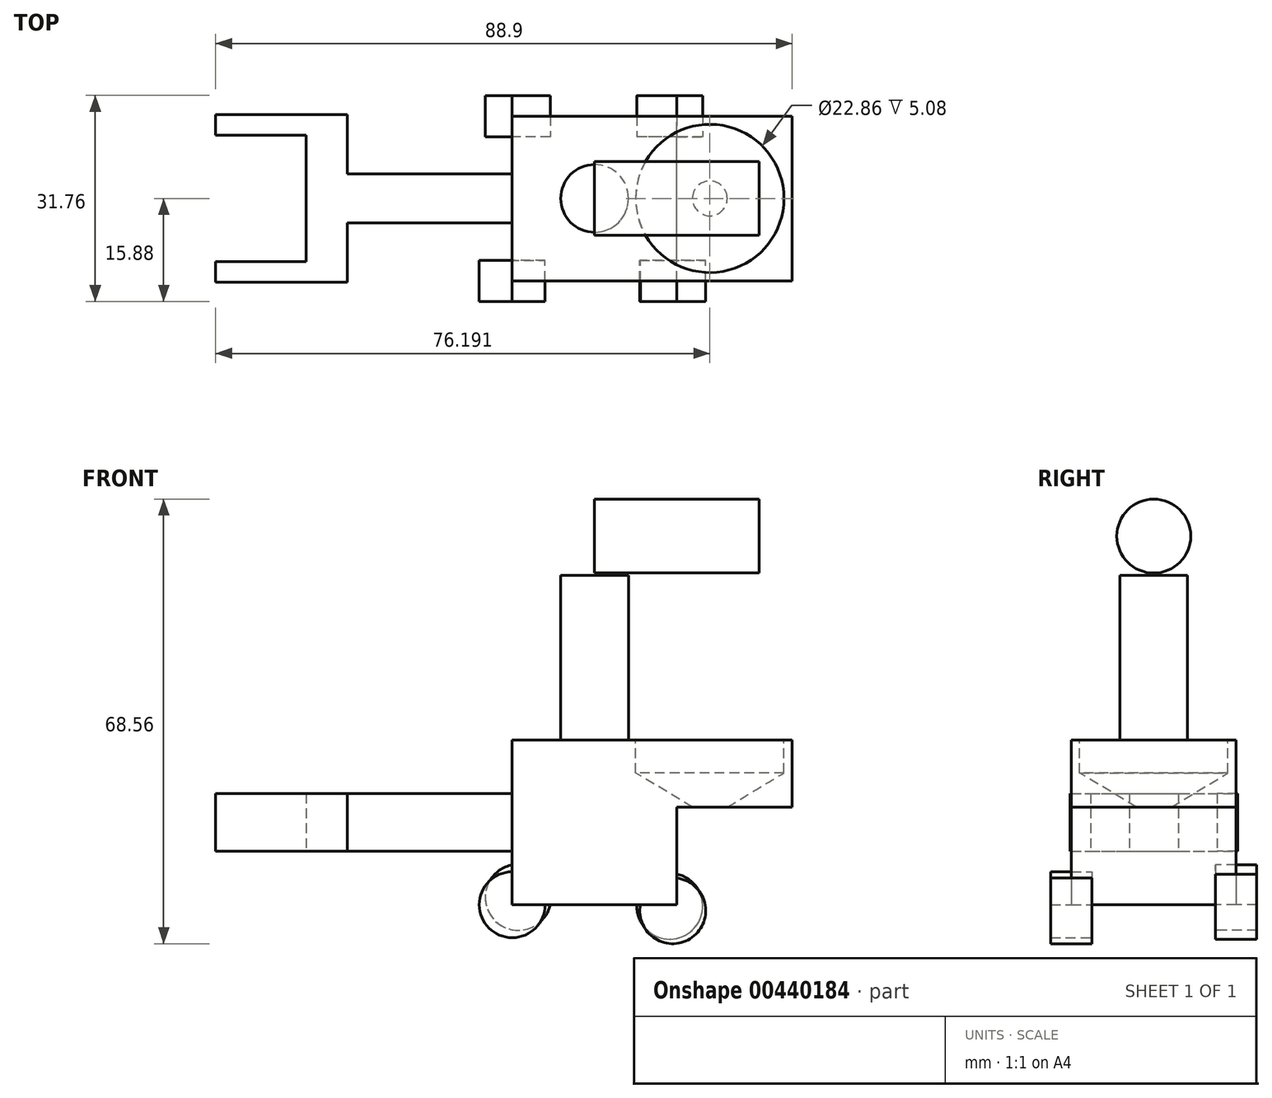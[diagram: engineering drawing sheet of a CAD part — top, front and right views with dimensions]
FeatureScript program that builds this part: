
annotation { "Feature Type Name" : "Feature", "Feature Type Description" : "" }
export const myFeature = defineFeature(function(context is Context, id is Id, definition is map)
    precondition{}
    {
        {
            var Q0;
            Q0=qCreatedBy(makeId("Front.planeOp"),FACE);
            var sketch = newSketch(context, id + "F0", { "sketchPlane" : qUnion([Q0])});
            skLineSegment(sketch, "E0.bottom", {"start": v(12.7, 12.7) * mm, "end": v(-12.7, 12.7) * mm});
            skLineSegment(sketch, "E0.top", {"start": v(12.7, -12.7) * mm, "end": v(-12.7, -12.7) * mm});
            skLineSegment(sketch, "E0.left", {"start": v(12.7, 12.7) * mm, "end": v(12.7, -12.7) * mm});
            skLineSegment(sketch, "E0.right", {"start": v(-12.7, 12.7) * mm, "end": v(-12.7, -12.7) * mm});
            skPoint(sketch, "E0.middle", {"position": v(0, 0) * mm});
            skSolve(sketch);
        }
        {
            var Q0;
            Q0=qSketchRegion(id+"F0",true);
            extrude(context, id + "F1", {"entities" : qUnion([Q0]), "endBound" : BoundingType.SYMMETRIC, "depth" : 25.4 * mm});
        }
        {
            var Q0;
            Q0=makeQuery(id+"F1.opExtrude","CAP_FACE",FACE,{"disambiguationData":[OSD([sQuery(id+"F0.wireOp",EDGE,"E0.bottom"),sQuery(id+"F0.wireOp",EDGE,"E0.top"),sQuery(id+"F0.wireOp",EDGE,"E0.left"),sQuery(id+"F0.wireOp",EDGE,"E0.right")])],"isStart":false});
            var sketch = newSketch(context, id + "F2", { "sketchPlane" : qUnion([Q0])});
            skCircle(sketch, "E1", {"center": v(-12.7, -12.7) * mm, "radius": 5.08 * mm});
            skCircle(sketch, "E2", {"center": v(12.06, -13.63) * mm, "radius": 5.08 * mm});
            skSolve(sketch);
        }
        {
            var Q0;
            {var subQ0=sQuery(id+"F2.wireOp",EDGE,"E1");var subQ1=makeQuery(id+"F1.opExtrude","CAP_EDGE",EDGE,{"disambiguationData":[OSD([sQuery(id+"F0.wireOp",EDGE,"E0.top")])],"isStart":false});var subQ2=makeQuery(id+"F2.imprint","INTERSECT",VERTEX,{"derivedFrom":[subQ1,subQ0]});Q0=makeQuery(id+"F2.imprint","IMPRINT",FACE,{"disambiguationData":[TD([[makeQuery(id+"F2.imprint","IMPRINT",EDGE,{"disambiguationData":[TD([[subQ2,1.0]])],"derivedFrom":subQ0}),1.0]])]});}
            var Q1;
            {var subQ0=sQuery(id+"F2.wireOp",EDGE,"E2");var subQ1=makeQuery(id+"F1.opExtrude","CAP_EDGE",EDGE,{"disambiguationData":[OSD([sQuery(id+"F0.wireOp",EDGE,"E0.top")])],"isStart":false});var subQ2=makeQuery(id+"F2.imprint","INTERSECT",VERTEX,{"derivedFrom":[subQ1,subQ0]});Q1=makeQuery(id+"F2.imprint","IMPRINT",FACE,{"disambiguationData":[TD([[makeQuery(id+"F2.imprint","IMPRINT",EDGE,{"disambiguationData":[TD([[subQ2,-1.0]])],"derivedFrom":subQ0}),1.0]])]});}
            extrude(context, id + "F3", {"entities" : qUnion([Q0, Q1]), "operationType" : NewBodyOperationType.ADD, "endBound" : BoundingType.SYMMETRIC, "depth" : 6.35 * mm});
        }
        {
            var Q0;
            Q0=makeQuery(id+"F1.opExtrude","CAP_FACE",FACE,{"disambiguationData":[OSD([sQuery(id+"F0.wireOp",EDGE,"E0.bottom"),sQuery(id+"F0.wireOp",EDGE,"E0.top"),sQuery(id+"F0.wireOp",EDGE,"E0.left"),sQuery(id+"F0.wireOp",EDGE,"E0.right")])],"isStart":true});
            var sketch = newSketch(context, id + "F4", { "sketchPlane" : qUnion([Q0])});
            skCircle(sketch, "E3", {"center": v(-11.6, -12.93) * mm, "radius": 5.08 * mm});
            skCircle(sketch, "E4", {"center": v(11.78, -11.56) * mm, "radius": 5.08 * mm});
            skSolve(sketch);
        }
        {
            var Q0;
            {var subQ0=sQuery(id+"F4.wireOp",EDGE,"E3");var subQ1=makeQuery(id+"F1.opExtrude","CAP_EDGE",EDGE,{"disambiguationData":[OSD([sQuery(id+"F0.wireOp",EDGE,"E0.top")])],"isStart":true});var subQ2=makeQuery(id+"F4.imprint","INTERSECT",VERTEX,{"derivedFrom":[subQ1,subQ0]});Q0=makeQuery(id+"F4.imprint","IMPRINT",FACE,{"disambiguationData":[TD([[makeQuery(id+"F4.imprint","IMPRINT",EDGE,{"disambiguationData":[TD([[subQ2,1.0]])],"derivedFrom":subQ0}),1.0]])]});}
            var Q1;
            {var subQ0=sQuery(id+"F4.wireOp",EDGE,"E4");var subQ1=makeQuery(id+"F1.opExtrude","CAP_EDGE",EDGE,{"disambiguationData":[OSD([sQuery(id+"F0.wireOp",EDGE,"E0.top")])],"isStart":true});var subQ2=makeQuery(id+"F4.imprint","INTERSECT",VERTEX,{"derivedFrom":[subQ1,subQ0]});Q1=makeQuery(id+"F4.imprint","IMPRINT",FACE,{"disambiguationData":[TD([[makeQuery(id+"F4.imprint","IMPRINT",EDGE,{"disambiguationData":[TD([[subQ2,-1.0]])],"derivedFrom":subQ0}),1.0]])]});}
            extrude(context, id + "F5", {"entities" : qUnion([Q0, Q1]), "operationType" : NewBodyOperationType.ADD, "endBound" : BoundingType.SYMMETRIC, "depth" : 6.35 * mm});
        }
        {
            var Q0;
            Q0=makeQuery(id+"F1.opExtrude","SWEPT_FACE",FACE,{"disambiguationData":[OSD([sQuery(id+"F0.wireOp",EDGE,"E0.bottom")])]});
            var sketch = newSketch(context, id + "F6", { "sketchPlane" : qUnion([Q0])});
            skCircle(sketch, "E5", {"center": v(0, 0) * mm, "radius": 5.22 * mm});
            skSolve(sketch);
        }
        {
            var Q0;
            Q0=makeQuery(id+"F6.imprint","IMPRINT",FACE,{"disambiguationData":[TD([[makeQuery(id+"F6.imprint","IMPRINT",EDGE,{"derivedFrom":sQuery(id+"F6.wireOp",EDGE,"E5")}),1.0]])]});
            extrude(context, id + "F7", {"entities" : qUnion([Q0]), "operationType" : NewBodyOperationType.ADD, "depth" : 25.4 * mm});
        }
        {
            var Q0;
            Q0=qCreatedBy(makeId("Right.planeOp"),FACE);
            var sketch = newSketch(context, id + "F8", { "sketchPlane" : qUnion([Q0])});
            skCircle(sketch, "E6", {"center": v(0, 44.15) * mm, "radius": 5.7 * mm});
            skSolve(sketch);
        }
        {
            var Q0;
            Q0=makeQuery(id+"F8.imprint","IMPRINT",FACE,{"disambiguationData":[TD([[makeQuery(id+"F8.imprint","IMPRINT",EDGE,{"derivedFrom":sQuery(id+"F8.wireOp",EDGE,"E6")}),1.0]])]});
            extrude(context, id + "F9", {"entities" : qUnion([Q0]), "depth" : 25.4 * mm});
        }
        {
            var Q0;
            Q0=makeQuery(id+"F1.opExtrude","SWEPT_FACE",FACE,{"disambiguationData":[OSD([sQuery(id+"F0.wireOp",EDGE,"E0.left")])]});
            var sketch = newSketch(context, id + "F10", { "sketchPlane" : qUnion([Q0])});
            skCircle(sketch, "E7", {"center": v(0, 0) * mm, "radius": 0.9 * mm});
            skSolve(sketch);
        }
        {
            var Q0;
            Q0=sQuery(id+"F10.wireOp",EDGE,"E7");
            extrude(context, id + "F11", {"bodyType" : ToolBodyType.SURFACE, "surfaceEntities" : qUnion([Q0]), "depth" : 25.4 * mm});
        }
        {
            var Q0;
            Q0=makeQuery(id+"F1.opExtrude","SWEPT_FACE",FACE,{"disambiguationData":[OSD([sQuery(id+"F0.wireOp",EDGE,"E0.right")])]});
            var sketch = newSketch(context, id + "F12", { "sketchPlane" : qUnion([Q0])});
            skLineSegment(sketch, "E8.bottom", {"start": v(3.8, 4.44) * mm, "end": v(-3.8, 4.44) * mm});
            skLineSegment(sketch, "E8.top", {"start": v(3.8, -4.44) * mm, "end": v(-3.8, -4.44) * mm});
            skLineSegment(sketch, "E8.left", {"start": v(3.8, 4.44) * mm, "end": v(3.8, -4.44) * mm});
            skLineSegment(sketch, "E8.right", {"start": v(-3.8, 4.44) * mm, "end": v(-3.8, -4.44) * mm});
            skPoint(sketch, "E8.middle", {"position": v(0, 0) * mm});
            skSolve(sketch);
        }
        {
            var Q0;
            Q0=makeQuery(id+"F12.imprint","IMPRINT",FACE,{"disambiguationData":[TD([[makeQuery(id+"F12.imprint","IMPRINT",EDGE,{"derivedFrom":sQuery(id+"F12.wireOp",EDGE,"E8.bottom")}),1.0]])]});
            extrude(context, id + "F13", {"entities" : qUnion([Q0]), "operationType" : NewBodyOperationType.ADD, "depth" : 25.4 * mm});
        }
        {
            var Q0;
            Q0=makeQuery(id+"F13.opExtrude","CAP_FACE",FACE,{"disambiguationData":[OSD([sQuery(id+"F12.wireOp",EDGE,"E8.bottom"),sQuery(id+"F12.wireOp",EDGE,"E8.top"),sQuery(id+"F12.wireOp",EDGE,"E8.left"),sQuery(id+"F12.wireOp",EDGE,"E8.right")])],"isStart":false});
            var sketch = newSketch(context, id + "F14", { "sketchPlane" : qUnion([Q0])});
            skLineSegment(sketch, "E9.bottom", {"start": v(9.75, 4.44) * mm, "end": v(-9.75, 4.44) * mm});
            skLineSegment(sketch, "E9.top", {"start": v(9.75, -4.44) * mm, "end": v(-9.75, -4.44) * mm});
            skLineSegment(sketch, "E9.left", {"start": v(9.75, 4.44) * mm, "end": v(9.75, -4.44) * mm});
            skLineSegment(sketch, "E9.right", {"start": v(-9.75, 4.44) * mm, "end": v(-9.75, -4.44) * mm});
            skPoint(sketch, "E9.middle", {"position": v(0, 0) * mm});
            skSolve(sketch);
        }
        {
            var Q0;
            {var subQ2=sQuery(id+"F14.wireOp",EDGE,"E9.right");Q0=makeQuery(id+"F14.imprint","IMPRINT",FACE,{"disambiguationData":[TD([[makeQuery(id+"F14.imprint","IMPRINT",EDGE,{"derivedFrom":subQ2}),1.0]])]});}
            var Q1;
            {var subQ1=makeQuery(id+"F13.opExtrude","CAP_EDGE",EDGE,{"disambiguationData":[OSD([sQuery(id+"F12.wireOp",EDGE,"E8.left")])],"isStart":false});Q1=makeQuery(id+"F14.imprint","IMPRINT",FACE,{"disambiguationData":[TD([[makeQuery(id+"F14.imprint","IMPRINT",EDGE,{"derivedFrom":subQ1}),-1.0]])]});}
            var Q2;
            {var subQ2=sQuery(id+"F14.wireOp",EDGE,"E9.left");Q2=makeQuery(id+"F14.imprint","IMPRINT",FACE,{"disambiguationData":[TD([[makeQuery(id+"F14.imprint","IMPRINT",EDGE,{"derivedFrom":subQ2}),-1.0]])]});}
            extrude(context, id + "F15", {"entities" : qUnion([Q0, Q1, Q2]), "operationType" : NewBodyOperationType.ADD, "depth" : 6.35 * mm});
        }
        {
            var Q0;
            Q0=makeQuery(id+"F15.opExtrude","SWEPT_FACE",FACE,{"disambiguationData":[OSD([sQuery(id+"F14.wireOp",EDGE,"E9.right")])]});
            var sketch = newSketch(context, id + "F16", { "sketchPlane" : qUnion([Q0])});
            skLineSegment(sketch, "E10.bottom", {"start": v(38.1, 4.44) * mm, "end": v(58.42, 4.44) * mm});
            skLineSegment(sketch, "E10.top", {"start": v(38.1, -4.44) * mm, "end": v(58.42, -4.44) * mm});
            skLineSegment(sketch, "E10.left", {"start": v(38.1, 4.44) * mm, "end": v(38.1, -4.44) * mm});
            skLineSegment(sketch, "E10.right", {"start": v(58.42, 4.44) * mm, "end": v(58.42, -4.44) * mm});
            skSolve(sketch);
        }
        {
            var Q0;
            {var subQ0=sQuery(id+"F16.wireOp",EDGE,"E10.left");Q0=makeQuery(id+"F16.imprint","IMPRINT",FACE,{"disambiguationData":[TD([[makeQuery(id+"F16.imprint","IMPRINT",EDGE,{"derivedFrom":subQ0}),1.0]])]});}
            var Q1;
            {var subQ2=sQuery(id+"F16.wireOp",EDGE,"E10.right");Q1=makeQuery(id+"F16.imprint","IMPRINT",FACE,{"disambiguationData":[TD([[makeQuery(id+"F16.imprint","IMPRINT",EDGE,{"derivedFrom":subQ2}),-1.0]])]});}
            extrude(context, id + "F17", {"entities" : qUnion([Q0, Q1]), "operationType" : NewBodyOperationType.ADD, "depth" : 3.17 * mm});
        }
        {
            var Q0;
            Q0=makeQuery(id+"F15.opExtrude","SWEPT_FACE",FACE,{"disambiguationData":[OSD([sQuery(id+"F14.wireOp",EDGE,"E9.left")])]});
            var sketch = newSketch(context, id + "F18", { "sketchPlane" : qUnion([Q0])});
            skLineSegment(sketch, "E11.bottom", {"start": v(-38.1, 4.44) * mm, "end": v(-58.42, 4.44) * mm});
            skLineSegment(sketch, "E11.top", {"start": v(-38.1, -4.44) * mm, "end": v(-58.42, -4.44) * mm});
            skLineSegment(sketch, "E11.left", {"start": v(-38.1, 4.44) * mm, "end": v(-38.1, -4.44) * mm});
            skLineSegment(sketch, "E11.right", {"start": v(-58.42, 4.44) * mm, "end": v(-58.42, -4.44) * mm});
            skSolve(sketch);
        }
        {
            var Q0;
            {var subQ2=sQuery(id+"F18.wireOp",EDGE,"E11.right");Q0=makeQuery(id+"F18.imprint","IMPRINT",FACE,{"disambiguationData":[TD([[makeQuery(id+"F18.imprint","IMPRINT",EDGE,{"derivedFrom":subQ2}),1.0]])]});}
            var Q1;
            {var subQ0=sQuery(id+"F18.wireOp",EDGE,"E11.left");Q1=makeQuery(id+"F18.imprint","IMPRINT",FACE,{"disambiguationData":[TD([[makeQuery(id+"F18.imprint","IMPRINT",EDGE,{"derivedFrom":subQ0}),-1.0]])]});}
            extrude(context, id + "F19", {"entities" : qUnion([Q0, Q1]), "operationType" : NewBodyOperationType.ADD, "depth" : 3.17 * mm});
        }
        {
            var Q0;
            Q0=makeQuery(id+"F1.opExtrude","SWEPT_FACE",FACE,{"disambiguationData":[OSD([sQuery(id+"F0.wireOp",EDGE,"E0.left")])]});
            var sketch = newSketch(context, id + "F20", { "sketchPlane" : qUnion([Q0])});
            skLineSegment(sketch, "E12.bottom", {"start": v(-12.7, 12.7) * mm, "end": v(12.7, 12.7) * mm});
            skLineSegment(sketch, "E12.top", {"start": v(-12.7, 2.36) * mm, "end": v(12.7, 2.36) * mm});
            skLineSegment(sketch, "E12.left", {"start": v(-12.7, 12.7) * mm, "end": v(-12.7, 2.36) * mm});
            skLineSegment(sketch, "E12.right", {"start": v(12.7, 12.7) * mm, "end": v(12.7, 2.36) * mm});
            skSolve(sketch);
        }
        {
            var Q0;
            Q0=makeQuery(id+"F20.imprint","IMPRINT",FACE,{"disambiguationData":[TD([[makeQuery(id+"F20.imprint","IMPRINT",EDGE,{"derivedFrom":sQuery(id+"F20.wireOp",EDGE,"E12.bottom")}),-1.0]])]});
            extrude(context, id + "F21", {"entities" : qUnion([Q0]), "operationType" : NewBodyOperationType.ADD, "depth" : 17.78 * mm});
        }
        {
            var Q0;
            Q0=makeQuery(id+"F21.boolean.opBoolean","MERGE",FACE,{"derivedFrom":[makeQuery(id+"F1.opExtrude","SWEPT_FACE",FACE,{"disambiguationData":[OSD([sQuery(id+"F0.wireOp",EDGE,"E0.bottom")])]}),makeQuery(id+"F21.opExtrude","SWEPT_FACE",FACE,{"disambiguationData":[OSD([sQuery(id+"F20.wireOp",EDGE,"E12.bottom")])]})]});
            var sketch = newSketch(context, id + "F22", { "sketchPlane" : qUnion([Q0])});
            skPoint(sketch, "E13.centerSnap0", {"position": v(30.48, 0) * mm});
            skCircle(sketch, "E14", {"center": v(17.77, 0) * mm, "radius": 11.86 * mm});
            skSolve(sketch);
        }
        {
            var Q0;
            Q0=sQuery(id+"F22.wireOp",VERTEX,"E14.center");
            var Q1;
            Q1=makeQuery(id+"F1.opExtrude","SWEPT_BODY",BODY,{"disambiguationData":[OSD([sQuery(id+"F0.wireOp",EDGE,"E0.bottom"),sQuery(id+"F0.wireOp",EDGE,"E0.top"),sQuery(id+"F0.wireOp",EDGE,"E0.left"),sQuery(id+"F0.wireOp",EDGE,"E0.right")])]});
            hole(context, id + "F23", {"style" : HoleStyle.SIMPLE, "endStyle" : HoleEndStyle.BLIND, "holeDiameter" : 22.86 * mm, "holeDepth" : 5.08 * mm, "isTappedThrough" : true, "tappedDepth" : 12.7 * mm, "tapClearance" : 3, "locations" : qUnion([Q0]), "scope" : qUnion([Q1])});
        }
        {
            var Q0;
            Q0=makeQuery(id+"F1.opExtrude","SWEPT_FACE",FACE,{"disambiguationData":[OSD([sQuery(id+"F0.wireOp",EDGE,"E0.right")])]});
            var sketch = newSketch(context, id + "F24", { "sketchPlane" : qUnion([Q0])});
            skCircle(sketch, "E15", {"center": v(-3.8, 8.54) * mm, "radius": 4.1 * mm});
            skCircle(sketch, "E16", {"center": v(5.05, 8.54) * mm, "radius": 4.35 * mm});
            skSolve(sketch);
        }
        {
            var Q0;
            Q0=sQuery(id+"F24.wireOp",EDGE,"E16");
            var Q1;
            Q1=sQuery(id+"F24.wireOp",EDGE,"E15");
            extrude(context, id + "F25", {"bodyType" : ToolBodyType.SURFACE, "surfaceEntities" : qUnion([Q0, Q1]), "depth" : 3.17 * mm});
        }
    });
